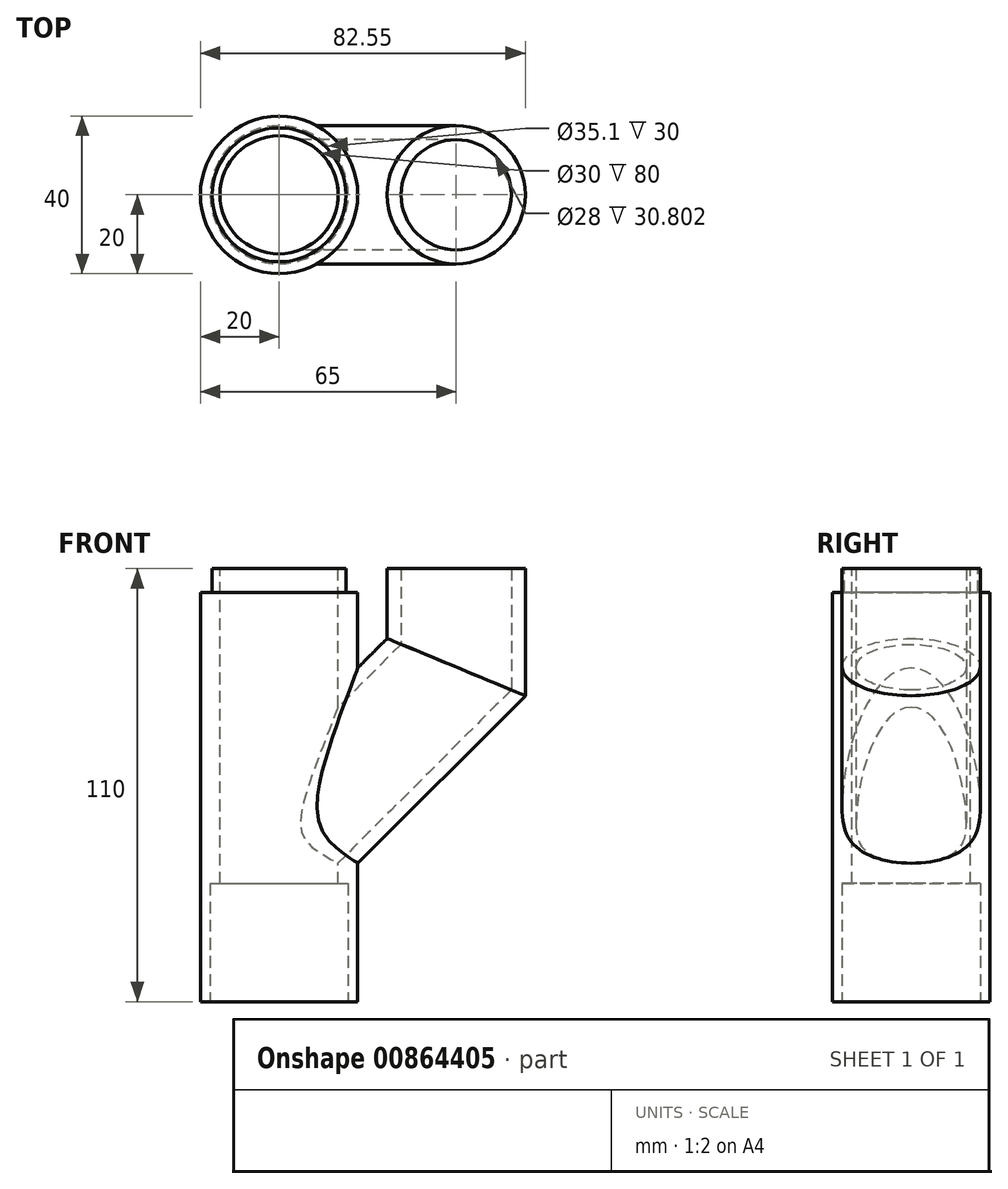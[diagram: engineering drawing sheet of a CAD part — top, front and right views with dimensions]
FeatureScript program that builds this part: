
annotation { "Feature Type Name" : "Feature", "Feature Type Description" : "" }
export const myFeature = defineFeature(function(context is Context, id is Id, definition is map)
    precondition{}
    {
        {
            var Q0;
            Q0=qCreatedBy(makeId("Front.planeOp"),FACE);
            var sketch = newSketch(context, id + "F0", { "sketchPlane" : qUnion([Q0])});
            skLineSegment(sketch, "E0", {"start": v(0, 0) * mm, "end": v(0, -70) * mm});
            skLineSegment(sketch, "E1", {"start": v(0, -70) * mm, "end": v(45, -25) * mm});
            skLineSegment(sketch, "E2", {"start": v(45, -25) * mm, "end": v(45, 0) * mm});
            skLineSegment(sketch, "E3", {"start": v(0, -70) * mm, "end": v(0, -110) * mm});
            skLineSegment(sketch, "E4", {"start": v(0, 0) * mm, "end": v(0, -25) * mm});
            skLineSegment(sketch, "E5", {"start": v(0, -25) * mm, "end": v(0, -70) * mm});
            skSolve(sketch);
        }
        {
            var Q0;
            Q0=qCreatedBy(makeId("Top.planeOp"),FACE);
            var sketch = newSketch(context, id + "F1", { "sketchPlane" : qUnion([Q0])});
            skCircle(sketch, "E6", {"center": v(0, 0) * mm, "radius": 20 * mm});
            skCircle(sketch, "E7", {"center": v(45, 0) * mm, "radius": 17.55 * mm});
            skSolve(sketch);
        }
        {
            var Q0;
            Q0=makeQuery(id+"F1.imprint","IMPRINT",FACE,{"disambiguationData":[TD([[makeQuery(id+"F1.imprint","IMPRINT",EDGE,{"derivedFrom":sQuery(id+"F1.wireOp",EDGE,"E6")}),1.0]])]});
            var Q1;
            Q1=sQuery(id+"F0.wireOp",EDGE,"E0");
            var Q2;
            Q2=sQuery(id+"F0.wireOp",EDGE,"E3");
            sweep(context, id + "F2", {"profiles" : qUnion([Q0]), "path" : qUnion([Q1, Q2])});
        }
        {
            var Q0;
            Q0=makeQuery(id+"F1.imprint","IMPRINT",FACE,{"disambiguationData":[TD([[makeQuery(id+"F1.imprint","IMPRINT",EDGE,{"derivedFrom":sQuery(id+"F1.wireOp",EDGE,"E7")}),1.0]])]});
            var Q1;
            Q1=sQuery(id+"F0.wireOp",EDGE,"E2");
            var Q2;
            Q2=sQuery(id+"F0.wireOp",EDGE,"E1");
            sweep(context, id + "F3", {"operationType" : NewBodyOperationType.ADD, "profiles" : qUnion([Q0]), "path" : qUnion([Q1, Q2])});
        }
        {
            var Q0;
            Q0=makeQuery(id+"F2.opSweep","CAP_FACE",FACE,{"disambiguationData":[OSD([sQuery(id+"F0.wireOp",VERTEX,"E3.end"),sQuery(id+"F1.wireOp",EDGE,"E6")])],"isStart":false});
            var sketch = newSketch(context, id + "F4", { "sketchPlane" : qUnion([Q0])});
            skCircle(sketch, "E8", {"center": v(0, 0) * mm, "radius": 17.55 * mm});
            skSolve(sketch);
        }
        {
            var Q0;
            Q0 = qSketchRegion(id + "F4", true);
            extrude(context, id + "F5", {"entities" : qUnion([Q0]), "operationType" : NewBodyOperationType.REMOVE, "oppositeDirection" : true, "depth" : 30 * mm, "offsetDistance" : 25 * mm});
        }
        {
            var Q0;
            Q0=makeQuery(id+"F1.imprint","IMPRINT",FACE,{"disambiguationData":[TD([[makeQuery(id+"F1.imprint","IMPRINT",EDGE,{"derivedFrom":sQuery(id+"F1.wireOp",EDGE,"E6")}),1.0]])]});
            var sketch = newSketch(context, id + "F6", { "sketchPlane" : qUnion([Q0])});
            skCircle(sketch, "E9", {"center": v(0, 0) * mm, "radius": 15 * mm});
            skSolve(sketch);
        }
        {
            var Q0;
            Q0=makeQuery(id+"F6.imprint","IMPRINT",FACE,{"disambiguationData":[TD([[makeQuery(id+"F6.imprint","IMPRINT",EDGE,{"derivedFrom":sQuery(id+"F6.wireOp",EDGE,"E9")}),1.0]])]});
            extrude(context, id + "F7", {"entities" : qUnion([Q0]), "operationType" : NewBodyOperationType.REMOVE, "endBound" : BoundingType.THROUGH_ALL, "oppositeDirection" : true, "depth" : 25 * mm, "offsetDistance" : 25 * mm});
        }
        {
            var Q0;
            Q0=makeQuery(id+"F1.imprint","IMPRINT",FACE,{"disambiguationData":[TD([[makeQuery(id+"F1.imprint","IMPRINT",EDGE,{"derivedFrom":sQuery(id+"F1.wireOp",EDGE,"E6")}),1.0]])]});
            var sketch = newSketch(context, id + "F8", { "sketchPlane" : qUnion([Q0])});
            skCircle(sketch, "E10", {"center": v(0, 0) * mm, "radius": 17 * mm});
            skCircle(sketch, "E11", {"center": v(0, 0) * mm, "radius": 20 * mm});
            skSolve(sketch);
        }
        {
            var Q0;
            Q0=makeQuery(id+"F8.imprint","IMPRINT",FACE,{"disambiguationData":[TD([[makeQuery(id+"F8.imprint","IMPRINT",EDGE,{"derivedFrom":sQuery(id+"F8.wireOp",EDGE,"E10")}),-1.0]])]});
            extrude(context, id + "F9", {"entities" : qUnion([Q0]), "operationType" : NewBodyOperationType.REMOVE, "oppositeDirection" : true, "depth" : 6 * mm, "offsetDistance" : 25 * mm});
        }
        {
            var Q0;
            Q0=makeQuery(id+"F1.imprint","IMPRINT",FACE,{"disambiguationData":[TD([[makeQuery(id+"F1.imprint","IMPRINT",EDGE,{"derivedFrom":sQuery(id+"F1.wireOp",EDGE,"E7")}),1.0]])]});
            var sketch = newSketch(context, id + "F10", { "sketchPlane" : qUnion([Q0])});
            skCircle(sketch, "E12", {"center": v(45, 0) * mm, "radius": 14 * mm});
            skSolve(sketch);
        }
        {
            var Q0;
            Q0=makeQuery(id+"F10.imprint","IMPRINT",FACE,{"disambiguationData":[TD([[makeQuery(id+"F10.imprint","IMPRINT",EDGE,{"derivedFrom":sQuery(id+"F10.wireOp",EDGE,"E12")}),1.0]])]});
            var Q1;
            Q1=sQuery(id+"F0.wireOp",EDGE,"E2");
            var Q2;
            Q2=sQuery(id+"F0.wireOp",EDGE,"E1");
            sweep(context, id + "F11", {"operationType" : NewBodyOperationType.REMOVE, "profiles" : qUnion([Q0]), "path" : qUnion([Q1, Q2])});
        }
    });
